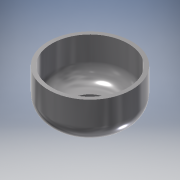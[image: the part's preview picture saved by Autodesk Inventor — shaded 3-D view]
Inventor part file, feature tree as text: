
AUTODESK INVENTOR PART (.ipt)
format: ipt  version: 2016 (Build 200138000, 138)  size: 344,064 bytes
history: native  units: mm
features: sketch x7, extrude x4, pattern_circular x3, projected_geometry x3, other x2, revolve x2, mirror x2, reference x2, thicken_offset x1, fillet x1, plane x1, hole x1
ambient origin geometry x8: Origin, YZ Plane, XZ Plane, XY Plane, X Axis, Y Axis, Z Axis, Center Point
bodies: Solid1 (feature_tree)
feature tree (29):
  other  "Fixture.ipt"
  other  "Transmission.ipt"
  revolve  "Revolution1"  [1 undecoded]
  sketch  "Sketch3"  dims[d4=3.0mm d5=90.0deg]
  extrude  "Extrusion1"  Depth=75.6mm
  extrude  "Extrusion2"  TaperAngle=90.0deg  [1 undecoded]
  mirror  "Mirror3"
  extrude  "Extrusion3"  Depth=10.0mm
  pattern_circular  "Circular Pattern1"  [2 undecoded]
  thicken_offset  "Thicken1"
  fillet  "Fillet1"  [1 undecoded]
  plane  "Work Plane3"
  hole  "Hole2"  [1 undecoded]
  revolve  "Revolution2"  [1 undecoded]
  sketch  "Sketch10"  dims[d9=22.2mm]
  pattern_circular  "Circular Pattern3"  Count=2 Angle=360.0deg
  pattern_circular  "Circular Pattern4"  [2 undecoded]
  mirror  "Mirror2"
  extrude  "Extrusion4"  Depth=4.5mm
  sketch  "Sketch1"  dims[d0=10.0mm d1=76.5mm]
  sketch  "Sketch2"  dims[d2=41.3mm d3=75.6mm]
  projected_geometry  "Projected Loop3"
  sketch  "Sketch4"  dims[d7=50.9mm d8=10.0mm]
  sketch  "Sketch11"  dims[d10=0.0mm]
  sketch  "Sketch12"  dims[d11=2.0mm d12=22.2mm d13=0.0mm d15=26.7mm d16=0.0mm d17=20.0mm d18=360.0deg d20=0.1mm d21=0.1mm d22=3.0mm d38=9.0mm d39=26.7mm d40=0.0mm d42=4.5mm d44=5.0mm d45=20.0mm d46=90.0deg d48=2.0mm d49=6.0mm d50=4.0mm d51=2.0mm d52=90.0deg d53=8.0mm d54=20.594885mm d55=30.0mm d56=11.524164mm d58=30.0mm d59=11.524164mm]
  projected_geometry  "Projected Loop7"
  projected_geometry  "Projected Loop8"
  reference  "Reference5"
  reference  "Reference6"
note: 9 required parameter values undecoded (feature->parameter linkage not recoverable at this tier; creation-order binding heuristic only, values carry confidence <= 0.55)